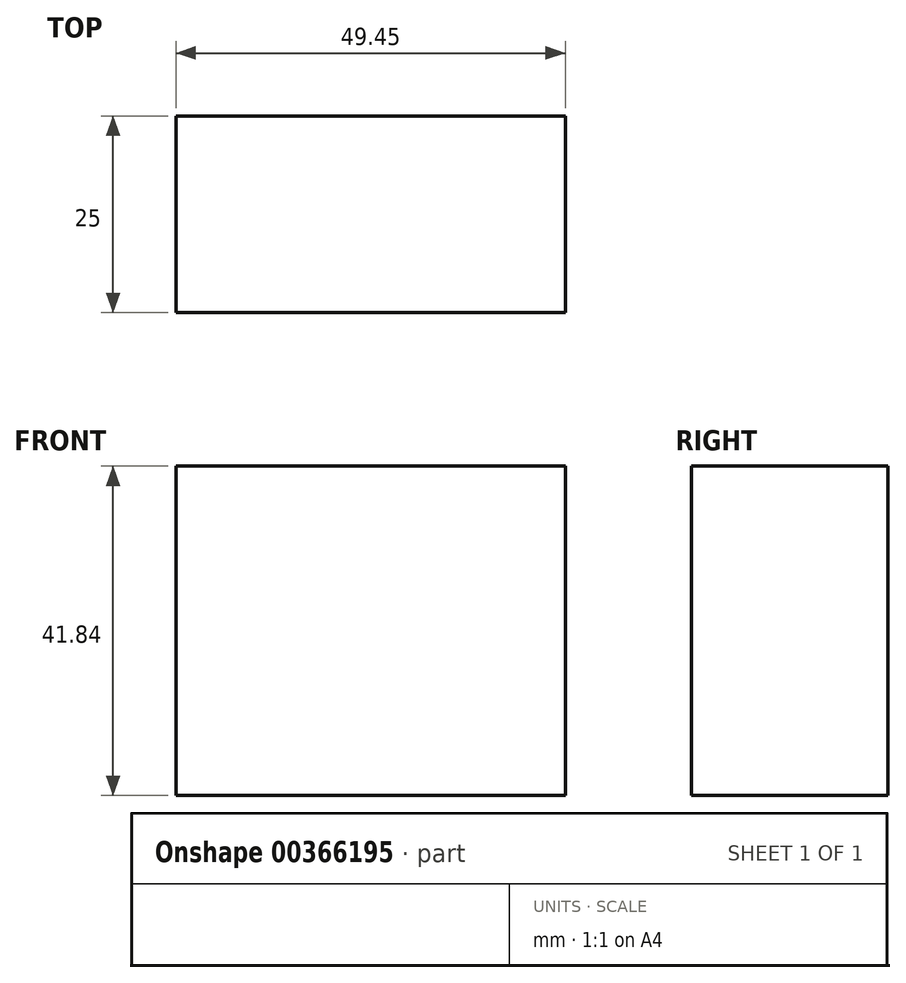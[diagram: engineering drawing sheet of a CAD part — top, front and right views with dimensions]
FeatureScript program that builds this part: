
annotation { "Feature Type Name" : "Feature", "Feature Type Description" : "" }
export const myFeature = defineFeature(function(context is Context, id is Id, definition is map)
    precondition{}
    {
        {
            var Q0;
            Q0=qCreatedBy(makeId("Front.planeOp"),FACE);
            var sketch = newSketch(context, id + "F0", { "sketchPlane" : qUnion([Q0])});
            skLineSegment(sketch, "E0.bottom", {"start": v(0, 71.82) * mm, "end": v(49.45, 71.82) * mm});
            skLineSegment(sketch, "E0.top", {"start": v(0, 29.98) * mm, "end": v(49.45, 29.98) * mm});
            skLineSegment(sketch, "E0.left", {"start": v(0, 71.82) * mm, "end": v(0, 29.98) * mm});
            skLineSegment(sketch, "E0.right", {"start": v(49.45, 71.82) * mm, "end": v(49.45, 29.98) * mm});
            skSolve(sketch);
        }
        {
            var Q0;
            Q0=makeQuery(id+"F0.imprint","IMPRINT",FACE,{"disambiguationData":[TD([[makeQuery(id+"F0.imprint","IMPRINT",EDGE,{"derivedFrom":sQuery(id+"F0.wireOp",EDGE,"E0.bottom")}),-1.0]])]});
            extrude(context, id + "F1", {"entities" : qUnion([Q0]), "depth" : 25 * mm});
        }
    });
